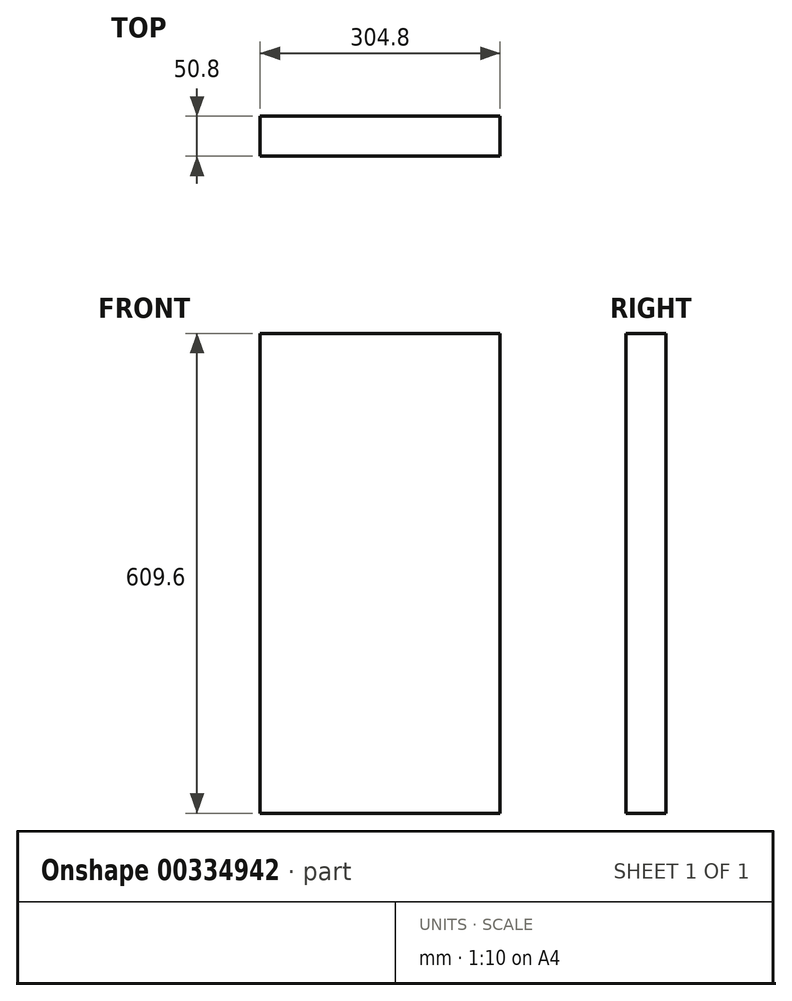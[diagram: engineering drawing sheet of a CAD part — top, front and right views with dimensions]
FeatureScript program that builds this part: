
annotation { "Feature Type Name" : "Feature", "Feature Type Description" : "" }
export const myFeature = defineFeature(function(context is Context, id is Id, definition is map)
    precondition{}
    {
        {
            var Q0;
            Q0=qCreatedBy(makeId("Front.planeOp"),FACE);
            var sketch = newSketch(context, id + "F0", { "sketchPlane" : qUnion([Q0])});
            skLineSegment(sketch, "E0.bottom", {"start": v(-276.47, 282.98) * mm, "end": v(28.33, 282.98) * mm});
            skLineSegment(sketch, "E0.top", {"start": v(-276.47, -326.62) * mm, "end": v(28.33, -326.62) * mm});
            skLineSegment(sketch, "E0.left", {"start": v(-276.47, 282.98) * mm, "end": v(-276.47, -326.62) * mm});
            skLineSegment(sketch, "E0.right", {"start": v(28.33, 282.98) * mm, "end": v(28.33, -326.62) * mm});
            skSolve(sketch);
        }
        {
            var Q0;
            Q0 = qSketchRegion(id + "F0", true);
            extrude(context, id + "F1", {"entities" : qUnion([Q0]), "depth" : 50.8 * mm});
        }
    });
